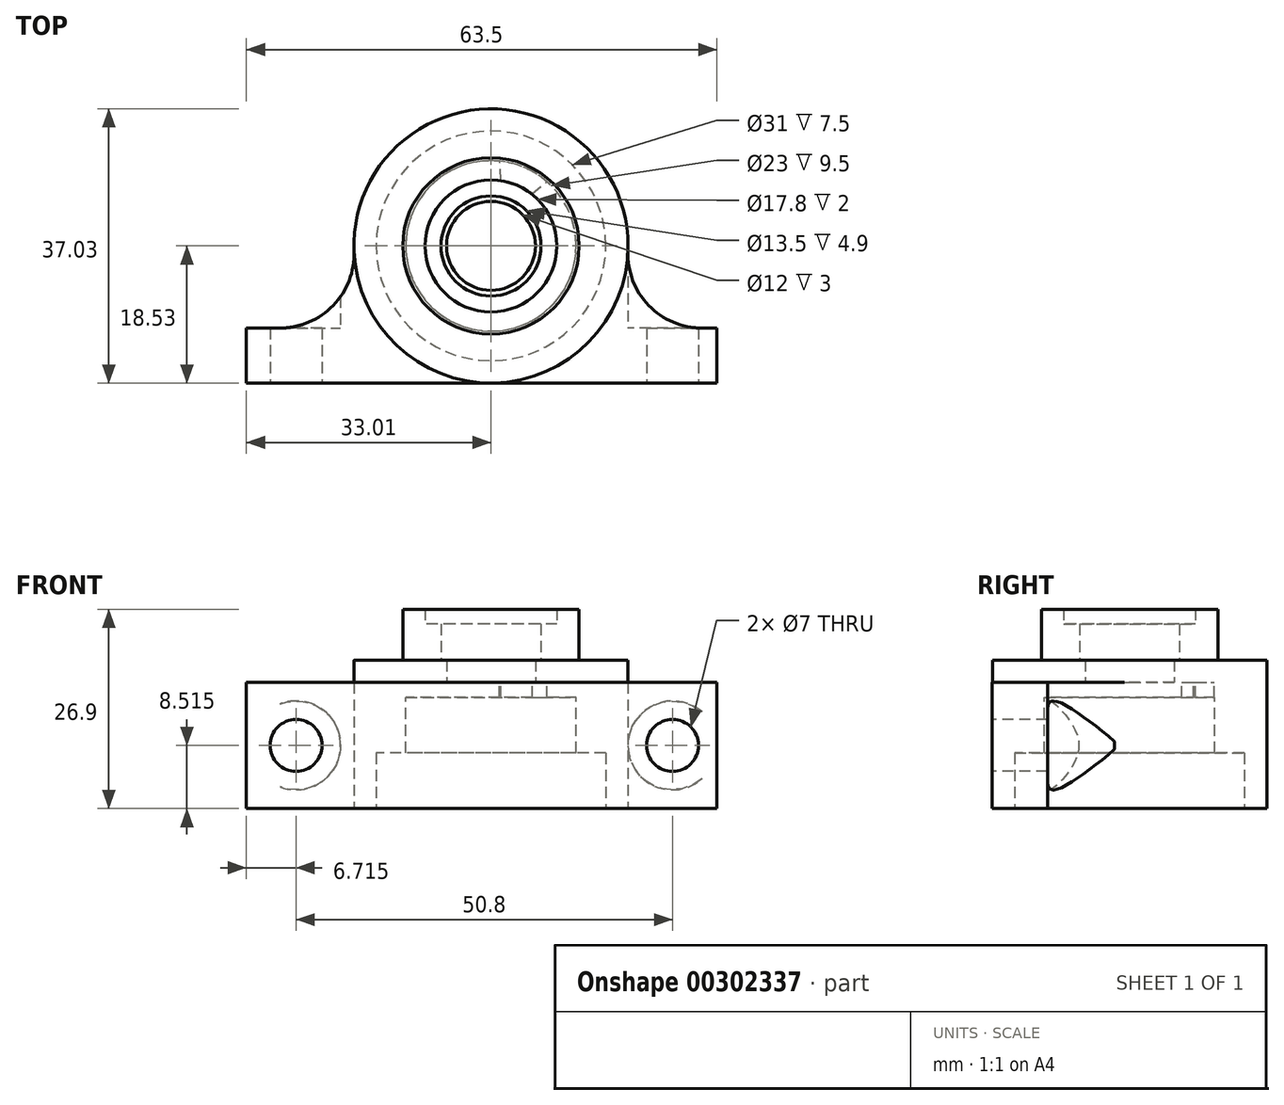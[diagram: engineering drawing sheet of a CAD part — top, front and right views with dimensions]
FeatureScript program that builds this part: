
annotation { "Feature Type Name" : "Feature", "Feature Type Description" : "" }
export const myFeature = defineFeature(function(context is Context, id is Id, definition is map)
    precondition{}
    {
        {
            var Q0;
            Q0=qCreatedBy(makeId("Top.planeOp"),FACE);
            var sketch = newSketch(context, id + "F0", { "sketchPlane" : qUnion([Q0])});
            skCircle(sketch, "E0", {"center": v(0, 0) * mm, "radius": 15.5 * mm});
            skCircle(sketch, "E1", {"center": v(0, 0) * mm, "radius": 18.5 * mm});
            skLineSegment(sketch, "E2.bottom", {"start": v(30.49, -15.5) * mm, "end": v(-33.01, -15.5) * mm});
            skLineSegment(sketch, "E2.top", {"start": v(30.49, -18.53) * mm, "end": v(-33.01, -18.53) * mm});
            skLineSegment(sketch, "E2.left", {"start": v(30.49, -15.5) * mm, "end": v(30.49, -18.53) * mm});
            skLineSegment(sketch, "E2.right", {"start": v(-33.01, -15.5) * mm, "end": v(-33.01, -18.53) * mm});
            skLineSegment(sketch, "E3.top", {"start": v(30.49, -11.09) * mm, "end": v(-33.01, -11.09) * mm});
            skLineSegment(sketch, "E3.left", {"start": v(30.49, -15.5) * mm, "end": v(30.49, -11.09) * mm});
            skLineSegment(sketch, "E3.right", {"start": v(-33.01, -15.5) * mm, "end": v(-33.01, -11.09) * mm});
            skSolve(sketch);
        }
        {
            var Q0;
            Q0=makeQuery(id+"F0.imprint","IMPRINT",FACE,{"disambiguationData":[TD([[makeQuery(id+"F0.imprint","IMPRINT",EDGE,{"derivedFrom":sQuery(id+"F0.wireOp",EDGE,"E0")}),-1.0]])]});
            var Q1;
            Q1=makeQuery(id+"F0.imprint","IMPRINT",FACE,{"disambiguationData":[TD([[makeQuery(id+"F0.imprint","IMPRINT",EDGE,{"derivedFrom":sQuery(id+"F0.wireOp",EDGE,"E2.top")}),-1.0]])]});
            var Q2;
            {var subQ0=sQuery(id+"F0.wireOp",EDGE,"E2.bottom");var subQ1=sQuery(id+"F0.wireOp",EDGE,"E1");var subQ2=makeQuery(id+"F0.imprint","INTERSECT",VERTEX,{"disambiguationData":[OD(0.0)],"derivedFrom":[subQ1,subQ0]});Q2=makeQuery(id+"F0.imprint","IMPRINT",FACE,{"disambiguationData":[TD([[makeQuery(id+"F0.imprint","IMPRINT",EDGE,{"disambiguationData":[TD([[subQ2,1.0]])],"derivedFrom":subQ1}),1.0]])]});}
            var Q3;
            {var subQ2=sQuery(id+"F0.wireOp",EDGE,"E1");var subQ4=sQuery(id+"F0.wireOp",EDGE,"E2.top");var subQ5=makeQuery(id+"F0.imprint","INTERSECT",VERTEX,{"disambiguationData":[OD(0.0)],"derivedFrom":[subQ2,subQ4]});Q3=makeQuery(id+"F0.imprint","IMPRINT",FACE,{"disambiguationData":[TD([[makeQuery(id+"F0.imprint","IMPRINT",EDGE,{"disambiguationData":[TD([[subQ5,1.0]])],"derivedFrom":subQ2}),1.0]])]});}
            var Q4;
            {var subQ5=sQuery(id+"F0.wireOp",EDGE,"E3.left");Q4=makeQuery(id+"F0.imprint","IMPRINT",FACE,{"disambiguationData":[TD([[makeQuery(id+"F0.imprint","IMPRINT",EDGE,{"derivedFrom":subQ5}),1.0]])]});}
            var Q5;
            {var subQ5=sQuery(id+"F0.wireOp",EDGE,"E3.right");Q5=makeQuery(id+"F0.imprint","IMPRINT",FACE,{"disambiguationData":[TD([[makeQuery(id+"F0.imprint","IMPRINT",EDGE,{"derivedFrom":subQ5}),-1.0]])]});}
            var Q6;
            {var subQ0=sQuery(id+"F0.wireOp",EDGE,"E2.bottom");var subQ1=sQuery(id+"F0.wireOp",EDGE,"E1");var subQ2=makeQuery(id+"F0.imprint","INTERSECT",VERTEX,{"disambiguationData":[OD(0.0)],"derivedFrom":[subQ1,subQ0]});Q6=makeQuery(id+"F0.imprint","IMPRINT",FACE,{"disambiguationData":[TD([[makeQuery(id+"F0.imprint","IMPRINT",EDGE,{"disambiguationData":[TD([[subQ2,-1.0]])],"derivedFrom":subQ1}),1.0]])]});}
            extrude(context, id + "F1", {"entities" : qUnion([Q0, Q1, Q2, Q3, Q4, Q5, Q6]), "depth" : 17 * mm});
        }
        {
            var Q0;
            Q0=makeQuery(id+"F1.opExtrude","CAP_FACE",FACE,{"disambiguationData":[OSD([sQuery(id+"F0.wireOp",EDGE,"E0"),sQuery(id+"F0.wireOp",EDGE,"E1")])],"isStart":false});
            var sketch = newSketch(context, id + "F2", { "sketchPlane" : qUnion([Q0])});
            skArc(sketch, "E4", {"start": v(1.36, 8.9) * mm, "mid": v(3.59, 8.25) * mm, "end": v(5.58, 7.06) * mm});
            skArc(sketch, "E5", {"start": v(-3.9, 3.12) * mm, "mid": v(-4.5, -2.17) * mm, "end": v(0, -5) * mm});
            skLineSegment(sketch, "E6", {"start": v(-3.9, 3.12) * mm, "end": v(-10.56, 11.35) * mm});
            skLineSegment(sketch, "E7", {"start": v(0, -5) * mm, "end": v(2, -15.37) * mm});
            skLineSegment(sketch, "E8", {"start": v(5.58, 7.06) * mm, "end": v(10.74, 11.17) * mm});
            skLineSegment(sketch, "E9", {"start": v(1.36, 8.9) * mm, "end": v(0.83, 15.48) * mm});
            skCircle(sketch, "E10", {"center": v(0, 0) * mm, "radius": 11.5 * mm});
            skSolve(sketch);
        }
        {
            var Q0;
            {var subQ0=sQuery(id+"F2.wireOp",EDGE,"E7");var subQ1=makeQuery(id+"F1.opExtrude","CAP_EDGE",EDGE,{"disambiguationData":[OSD([sQuery(id+"F0.wireOp",EDGE,"E0")])],"isStart":false});var subQ2=makeQuery(id+"F2.imprint","INTERSECT",VERTEX,{"derivedFrom":[subQ1,subQ0]});Q0=makeQuery(id+"F2.imprint","IMPRINT",FACE,{"disambiguationData":[TD([[makeQuery(id+"F2.imprint","IMPRINT",EDGE,{"disambiguationData":[TD([[subQ2,1.0]])],"derivedFrom":subQ0}),1.0]])]});}
            var Q1;
            {var subQ0=sQuery(id+"F2.wireOp",EDGE,"E8");var subQ1=makeQuery(id+"F1.opExtrude","CAP_EDGE",EDGE,{"disambiguationData":[OSD([sQuery(id+"F0.wireOp",EDGE,"E0")])],"isStart":false});var subQ2=makeQuery(id+"F2.imprint","INTERSECT",VERTEX,{"derivedFrom":[subQ1,subQ0]});Q1=makeQuery(id+"F2.imprint","IMPRINT",FACE,{"disambiguationData":[TD([[makeQuery(id+"F2.imprint","IMPRINT",EDGE,{"disambiguationData":[TD([[subQ2,1.0]])],"derivedFrom":subQ0}),1.0]])]});}
            var Q2;
            {var subQ0=sQuery(id+"F2.wireOp",EDGE,"E6");var subQ1=makeQuery(id+"F1.opExtrude","CAP_EDGE",EDGE,{"disambiguationData":[OSD([sQuery(id+"F0.wireOp",EDGE,"E0")])],"isStart":false});var subQ2=makeQuery(id+"F2.imprint","INTERSECT",VERTEX,{"derivedFrom":[subQ1,subQ0]});Q2=makeQuery(id+"F2.imprint","IMPRINT",FACE,{"disambiguationData":[TD([[makeQuery(id+"F2.imprint","IMPRINT",EDGE,{"disambiguationData":[TD([[subQ2,1.0]])],"derivedFrom":subQ0}),-1.0]])]});}
            var Q3;
            {var subQ0=sQuery(id+"F2.wireOp",EDGE,"E6");var subQ1=makeQuery(id+"F1.opExtrude","CAP_EDGE",EDGE,{"disambiguationData":[OSD([sQuery(id+"F0.wireOp",EDGE,"E0")])],"isStart":false});var subQ2=makeQuery(id+"F2.imprint","INTERSECT",VERTEX,{"derivedFrom":[subQ1,subQ0]});Q3=makeQuery(id+"F2.imprint","IMPRINT",FACE,{"disambiguationData":[TD([[makeQuery(id+"F2.imprint","IMPRINT",EDGE,{"disambiguationData":[TD([[subQ2,1.0]])],"derivedFrom":subQ0}),1.0]])]});}
            extrude(context, id + "F3", {"entities" : qUnion([Q0, Q1, Q2, Q3]), "oppositeDirection" : true, "depth" : 9.5 * mm});
        }
        {
            var Q0;
            {var subQ0=sQuery(id+"F2.wireOp",EDGE,"E5");Q0=makeQuery(id+"F2.imprint","IMPRINT",FACE,{"disambiguationData":[TD([[makeQuery(id+"F2.imprint","IMPRINT",EDGE,{"derivedFrom":subQ0}),-1.0]])]});}
            var Q1;
            {var subQ0=sQuery(id+"F2.wireOp",EDGE,"E4");Q1=makeQuery(id+"F2.imprint","IMPRINT",FACE,{"disambiguationData":[TD([[makeQuery(id+"F2.imprint","IMPRINT",EDGE,{"derivedFrom":subQ0}),1.0]])]});}
            extrude(context, id + "F4", {"entities" : qUnion([Q0, Q1]), "operationType" : NewBodyOperationType.ADD, "oppositeDirection" : true, "depth" : 2 * mm});
        }
        {
            var Q0;
            Q0=makeQuery(id+"F1.opExtrude","CAP_FACE",FACE,{"disambiguationData":[OSD([sQuery(id+"F0.wireOp",EDGE,"E0"),sQuery(id+"F0.wireOp",EDGE,"E1"),sQuery(id+"F0.wireOp",EDGE,"E2.top"),sQuery(id+"F0.wireOp",EDGE,"E2.left"),sQuery(id+"F0.wireOp",EDGE,"E2.right"),sQuery(id+"F0.wireOp",EDGE,"E3.top"),sQuery(id+"F0.wireOp",EDGE,"E3.left"),sQuery(id+"F0.wireOp",EDGE,"E3.right")])],"isStart":false});
            var sketch = newSketch(context, id + "F5", { "sketchPlane" : qUnion([Q0])});
            skCircle(sketch, "E11", {"center": v(0, 0) * mm, "radius": 6 * mm});
            skCircle(sketch, "E12", {"center": v(0, 0) * mm, "radius": 18.5 * mm});
            skSolve(sketch);
        }
        {
            var Q0;
            Q0=makeQuery(id+"F5.imprint","IMPRINT",FACE,{"disambiguationData":[TD([[makeQuery(id+"F5.imprint","IMPRINT",EDGE,{"derivedFrom":sQuery(id+"F5.wireOp",EDGE,"E11")}),-1.0]])]});
            var Q1;
            Q1=makeQuery(id+"F5.imprint","IMPRINT",FACE,{"disambiguationData":[TD([[makeQuery(id+"F5.imprint","IMPRINT",EDGE,{"derivedFrom":makeQuery(id+"F1.opExtrude","CAP_EDGE",EDGE,{"disambiguationData":[OSD([sQuery(id+"F0.wireOp",EDGE,"E0")])],"isStart":false})}),-1.0]])]});
            extrude(context, id + "F6", {"entities" : qUnion([Q0, Q1]), "operationType" : NewBodyOperationType.ADD, "depth" : 3 * mm});
        }
        {
            var Q0;
            Q0=makeQuery(id+"F6.opExtrude","CAP_FACE",FACE,{"disambiguationData":[OSD([sQuery(id+"F5.wireOp",EDGE,"E11"),sQuery(id+"F5.wireOp",EDGE,"E12")])],"isStart":false});
            var sketch = newSketch(context, id + "F7", { "sketchPlane" : qUnion([Q0])});
            skCircle(sketch, "E13", {"center": v(0, 0) * mm, "radius": 8.9 * mm});
            skCircle(sketch, "E14", {"center": v(0, 0) * mm, "radius": 11.9 * mm});
            skCircle(sketch, "E15", {"center": v(0, 0) * mm, "radius": 6.75 * mm});
            skSolve(sketch);
        }
        {
            var Q0;
            Q0=makeQuery(id+"F7.imprint","IMPRINT",FACE,{"disambiguationData":[TD([[makeQuery(id+"F7.imprint","IMPRINT",EDGE,{"derivedFrom":sQuery(id+"F7.wireOp",EDGE,"E13")}),-1.0]])]});
            extrude(context, id + "F8", {"entities" : qUnion([Q0]), "operationType" : NewBodyOperationType.ADD, "depth" : 6.9 * mm});
        }
        {
            var Q0;
            {var subQ0=sQuery(id+"F0.wireOp",EDGE,"E3.top");var subQ1=sQuery(id+"F0.wireOp",EDGE,"E1");Q0=makeQuery(id+"F1.opExtrude","SWEPT_EDGE",EDGE,{"disambiguationData":[OSD([subQ1,subQ0]),TDD([makeQuery(id+"F0.imprint","INTERSECT",VERTEX,{"disambiguationData":[OD(1.0)],"derivedFrom":[subQ1,subQ0]})])]});}
            var Q1;
            {var subQ0=sQuery(id+"F0.wireOp",EDGE,"E3.top");var subQ1=sQuery(id+"F0.wireOp",EDGE,"E1");Q1=makeQuery(id+"F1.opExtrude","SWEPT_EDGE",EDGE,{"disambiguationData":[OSD([subQ1,subQ0]),TDD([makeQuery(id+"F0.imprint","INTERSECT",VERTEX,{"disambiguationData":[OD(0.0)],"derivedFrom":[subQ1,subQ0]})])]});}
            fillet(context, id + "F9", {"entities" : qUnion([Q0, Q1]), "radius" : 10 * mm, "tangentPropagation" : true, "allowEdgeOverflow" : false});
        }
        {
            var Q0;
            {var subQ0=sQuery(id+"F0.wireOp",EDGE,"E2.top");Q0=makeQuery(id+"FF00v4OMAmH5S7i_1.boolean.opBoolean","MERGE",FACE,{"derivedFrom":[makeQuery(id+"F1.opExtrude","SWEPT_FACE",FACE,{"disambiguationData":[OSD([subQ0])]}),makeQuery(id+"FF00v4OMAmH5S7i_1.opExtrude","SWEPT_FACE",FACE,{"disambiguationData":[OSD([subQ0])]})]});}
            var sketch = newSketch(context, id + "F10", { "sketchPlane" : qUnion([Q0])});
            skCircle(sketch, "E16", {"center": v(-26.3, 8.51) * mm, "radius": 3.5 * mm});
            skCircle(sketch, "E17", {"center": v(24.5, 8.51) * mm, "radius": 3.5 * mm});
            skSolve(sketch);
        }
        {
            var Q0;
            Q0=makeQuery(id+"F10.imprint","IMPRINT",FACE,{"disambiguationData":[TD([[makeQuery(id+"F10.imprint","IMPRINT",EDGE,{"derivedFrom":sQuery(id+"F10.wireOp",EDGE,"E16")}),1.0]])]});
            var Q1;
            Q1=makeQuery(id+"F10.imprint","IMPRINT",FACE,{"disambiguationData":[TD([[makeQuery(id+"F10.imprint","IMPRINT",EDGE,{"derivedFrom":sQuery(id+"F10.wireOp",EDGE,"E17")}),1.0]])]});
            extrude(context, id + "F11", {"entities" : qUnion([Q0, Q1]), "operationType" : NewBodyOperationType.REMOVE, "endBound" : BoundingType.THROUGH_ALL, "oppositeDirection" : true, "depth" : 25 * mm});
        }
        {
            var Q0;
            {var subQ0=sQuery(id+"F0.wireOp",EDGE,"E3.top");Q0=makeQuery(id+"F1.opExtrude","SWEPT_FACE",FACE,{"disambiguationData":[OSD([subQ0]),TDD([makeQuery(id+"F0.imprint","IMPRINT",EDGE,{"disambiguationData":[TD([[makeQuery(id+"F0.imprint","INTERSECT",VERTEX,{"derivedFrom":[subQ0,sQuery(id+"F0.wireOp",EDGE,"E3.right")]}),1.0]])],"derivedFrom":subQ0})])]});}
            var sketch = newSketch(context, id + "F12", { "sketchPlane" : qUnion([Q0])});
            skCircle(sketch, "E18", {"center": v(26.3, 8.51) * mm, "radius": 6 * mm});
            skSolve(sketch);
        }
        {
            var Q0;
            Q0=makeQuery(id+"F12.imprint","IMPRINT",FACE,{"disambiguationData":[TD([[makeQuery(id+"F12.imprint","IMPRINT",EDGE,{"derivedFrom":sQuery(id+"F12.wireOp",EDGE,"E18")}),1.0]])]});
            extrude(context, id + "F13", {"entities" : qUnion([Q0]), "operationType" : NewBodyOperationType.REMOVE, "endBound" : BoundingType.THROUGH_ALL, "depth" : 25 * mm});
        }
        {
            var Q0;
            {var subQ0=sQuery(id+"F0.wireOp",EDGE,"E3.top");var subQ1=makeQuery(id+"F0.imprint","IMPRINT",EDGE,{"disambiguationData":[TD([[makeQuery(id+"F0.imprint","INTERSECT",VERTEX,{"derivedFrom":[subQ0,sQuery(id+"F0.wireOp",EDGE,"E3.left")]}),-1.0]])],"derivedFrom":subQ0});Q0=makeQuery(id+"FF00v4OMAmH5S7i_1.boolean.opBoolean","MERGE",FACE,{"derivedFrom":[makeQuery(id+"F1.opExtrude","SWEPT_FACE",FACE,{"disambiguationData":[OSD([subQ0]),TDD([subQ1])]}),makeQuery(id+"FF00v4OMAmH5S7i_1.opExtrude","SWEPT_FACE",FACE,{"disambiguationData":[OSD([subQ0]),TDD([makeQuery(id+"F2.imprint","IMPRINT",EDGE,{"derivedFrom":makeQuery(id+"F1.opExtrude","CAP_EDGE",EDGE,{"disambiguationData":[OSD([subQ0]),TDD([subQ1])],"isStart":false})})])]})]});}
            var sketch = newSketch(context, id + "F14", { "sketchPlane" : qUnion([Q0])});
            skCircle(sketch, "E19", {"center": v(-24.5, 8.51) * mm, "radius": 6 * mm});
            skSolve(sketch);
        }
        {
            var Q0;
            {var subQ0=sQuery(id+"F14.wireOp",EDGE,"E19");var subQ1=sQuery(id+"F0.wireOp",EDGE,"E3.top");var subQ2=sQuery(id+"F0.wireOp",EDGE,"E1");var subQ3=makeQuery(id+"F0.imprint","INTERSECT",VERTEX,{"disambiguationData":[OD(1.0)],"derivedFrom":[subQ2,subQ1]});var subQ4=makeQuery(id+"F0.imprint","IMPRINT",EDGE,{"disambiguationData":[TD([[makeQuery(id+"F0.imprint","INTERSECT",VERTEX,{"derivedFrom":[subQ1,sQuery(id+"F0.wireOp",EDGE,"E3.left")]}),-1.0]])],"derivedFrom":subQ1});var subQ5=makeQuery(id+"F1.opExtrude","CAP_EDGE",EDGE,{"disambiguationData":[OSD([subQ1]),TDD([subQ4])],"isStart":false});var subQ6=makeQuery(id+"F9.opFillet","BLEND_EDGE",EDGE,{"blendedFrom":[makeQuery(id+"FF00v4OMAmH5S7i_1.boolean.opBoolean","MERGE",EDGE,{"derivedFrom":[makeQuery(id+"F1.opExtrude","SWEPT_EDGE",EDGE,{"disambiguationData":[OSD([subQ2,subQ1]),TDD([subQ3])]}),makeQuery(id+"FF00v4OMAmH5S7i_1.opExtrude","SWEPT_EDGE",EDGE,{"disambiguationData":[OSD([subQ2,subQ1]),TDD([makeQuery(id+"F2.imprint","INTERSECT",VERTEX,{"derivedFrom":[makeQuery(id+"F1.opExtrude","CAP_EDGE",EDGE,{"disambiguationData":[OSD([subQ2])],"isStart":false}),subQ5]})])]})]}),makeQuery(id+"FF00v4OMAmH5S7i_1.boolean.opBoolean","MERGE",FACE,{"derivedFrom":[makeQuery(id+"F1.opExtrude","SWEPT_FACE",FACE,{"disambiguationData":[OSD([subQ1]),TDD([subQ4])]}),makeQuery(id+"FF00v4OMAmH5S7i_1.opExtrude","SWEPT_FACE",FACE,{"disambiguationData":[OSD([subQ1]),TDD([makeQuery(id+"F2.imprint","IMPRINT",EDGE,{"derivedFrom":subQ5})])]})]})],"blendedInto":[makeQuery(id+"FF00v4OMAmH5S7i_1.boolean.opBoolean","MERGE",FACE,{"derivedFrom":[makeQuery(id+"F1.opExtrude","SWEPT_FACE",FACE,{"disambiguationData":[OSD([subQ1]),TDD([subQ4])]}),makeQuery(id+"FF00v4OMAmH5S7i_1.opExtrude","SWEPT_FACE",FACE,{"disambiguationData":[OSD([subQ1]),TDD([makeQuery(id+"F2.imprint","IMPRINT",EDGE,{"derivedFrom":subQ5})])]})]})]});var subQ7=makeQuery(id+"F14.imprint","INTERSECT",VERTEX,{"disambiguationData":[OD(0.0)],"derivedFrom":[subQ6,subQ0]});Q0=makeQuery(id+"F14.imprint","IMPRINT",FACE,{"disambiguationData":[TD([[makeQuery(id+"F14.imprint","IMPRINT",EDGE,{"disambiguationData":[TD([[subQ7,1.0]])],"derivedFrom":subQ0}),1.0]])]});}
            extrude(context, id + "F15", {"entities" : qUnion([Q0]), "operationType" : NewBodyOperationType.REMOVE, "endBound" : BoundingType.THROUGH_ALL, "depth" : 25 * mm});
        }
        {
            var Q0;
            Q0=makeQuery(id+"F7.imprint","IMPRINT",FACE,{"disambiguationData":[TD([[makeQuery(id+"F7.imprint","IMPRINT",EDGE,{"derivedFrom":sQuery(id+"F7.wireOp",EDGE,"E13")}),1.0]])]});
            extrude(context, id + "F16", {"entities" : qUnion([Q0]), "operationType" : NewBodyOperationType.ADD, "depth" : 4.9 * mm});
        }
    });
